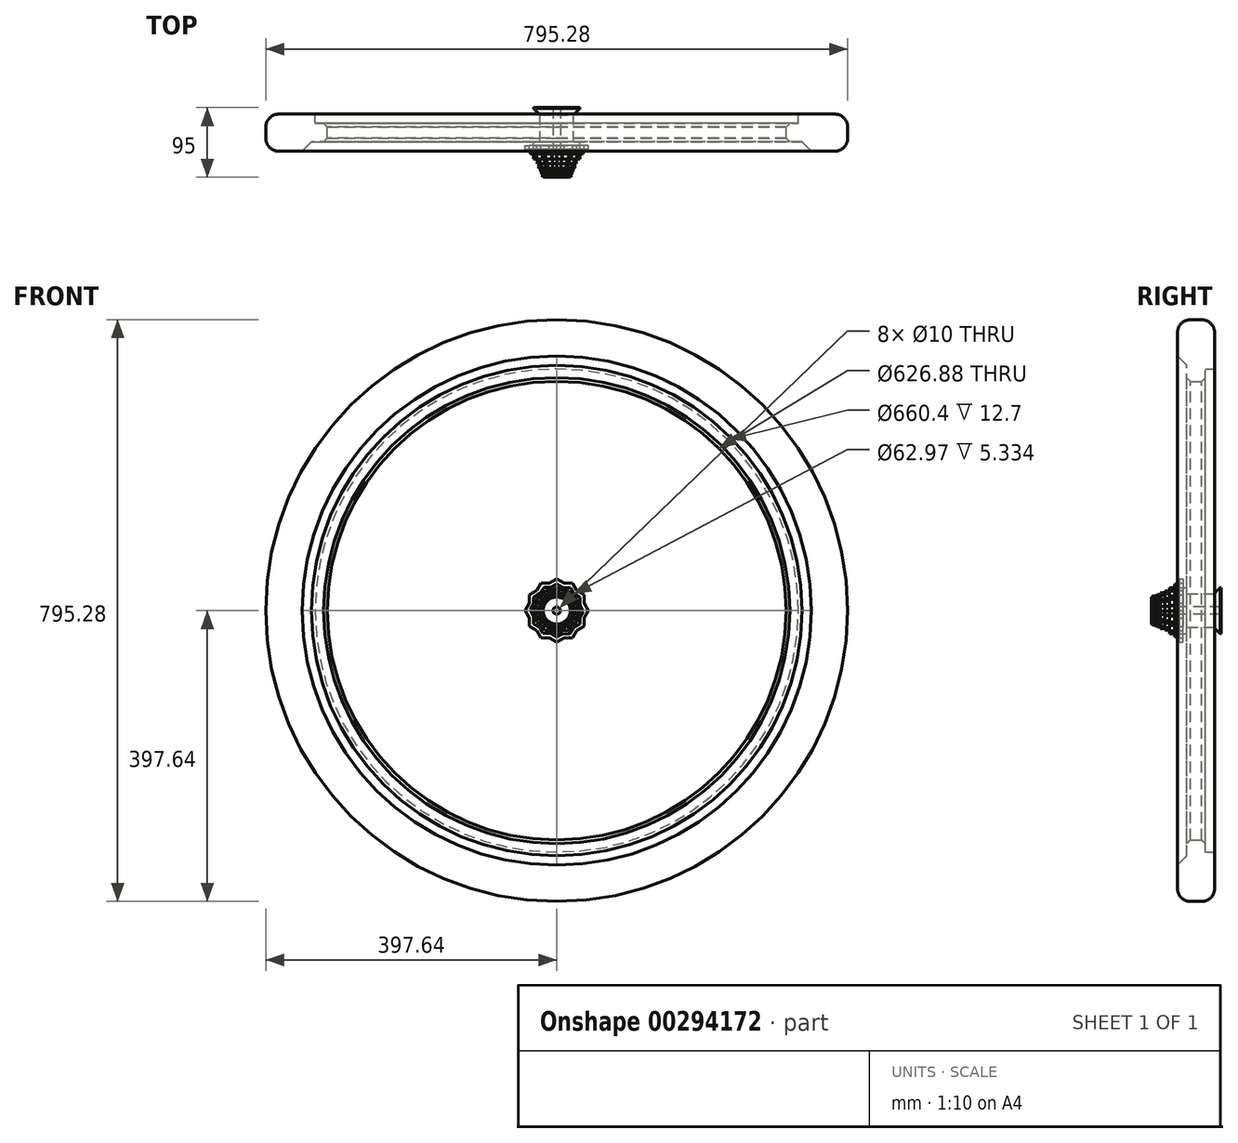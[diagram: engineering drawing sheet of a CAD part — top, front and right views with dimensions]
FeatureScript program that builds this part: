
annotation { "Feature Type Name" : "Feature", "Feature Type Description" : "" }
export const myFeature = defineFeature(function(context is Context, id is Id, definition is map)
    precondition{}
    {
        {
            var Q0;
            Q0=qCreatedBy(makeId("Front.planeOp"),FACE);
            var sketch = newSketch(context, id + "F0", { "sketchPlane" : qUnion([Q0])});
            skCircle(sketch, "E0", {"center": v(0, 0) * mm, "radius": 330.2 * mm});
            skCircle(sketch, "E1", {"center": v(0, 0) * mm, "radius": 313.44 * mm});
            skSolve(sketch);
        }
        {
            var Q0;
            Q0 = qSketchRegion(id + "F0", true);
            extrude(context, id + "F1", {"entities" : qUnion([Q0]), "endBound" : BoundingType.SYMMETRIC, "depth" : 25.4 * mm});
        }
        {
            var Q0;
            Q0=makeQuery(id+"F1.opExtrude","CAP_EDGE",EDGE,{"disambiguationData":[OSD([sQuery(id+"F0.wireOp",EDGE,"E1")])],"isStart":false});
            var Q1;
            Q1=makeQuery(id+"F1.opExtrude","CAP_EDGE",EDGE,{"disambiguationData":[OSD([sQuery(id+"F0.wireOp",EDGE,"E1")])],"isStart":true});
            chamfer(context, id + "F2", {"entities" : qUnion([Q0, Q1]), "width" : 5.08 * mm, "tangentPropagation" : true});
        }
        {
            var Q0;
            Q0=qCreatedBy(makeId("Front.planeOp"),FACE);
            var sketch = newSketch(context, id + "F3", { "sketchPlane" : qUnion([Q0])});
            skCircle(sketch, "E2", {"center": v(0, 0) * mm, "radius": 23.03 * mm});
            skSolve(sketch);
        }
        {
            var Q0;
            Q0 = qSketchRegion(id + "F3", true);
            extrude(context, id + "F4", {"entities" : qUnion([Q0]), "endBound" : BoundingType.SYMMETRIC, "depth" : 25.4 * mm});
        }
        {
            var Q0;
            Q0=makeQuery(id+"F4.opExtrude","CAP_FACE",FACE,{"disambiguationData":[OSD([sQuery(id+"F3.wireOp",EDGE,"E2")])],"isStart":true});
            var sketch = newSketch(context, id + "F5", { "sketchPlane" : qUnion([Q0])});
            skCircle(sketch, "E3", {"center": v(0, 0) * mm, "radius": 31.49 * mm});
            skSolve(sketch);
        }
        {
            var Q0;
            Q0 = qSketchRegion(id + "F5", true);
            extrude(context, id + "F6", {"entities" : qUnion([Q0]), "operationType" : NewBodyOperationType.ADD, "depth" : 21.59 * mm});
        }
        {
            var Q0;
            Q0=makeQuery(id+"F4.opExtrude","CAP_FACE",FACE,{"disambiguationData":[OSD([sQuery(id+"F3.wireOp",EDGE,"E2")])],"isStart":false});
            var sketch = newSketch(context, id + "F7", { "sketchPlane" : qUnion([Q0])});
            skCircle(sketch, "E4", {"center": v(0, 0) * mm, "radius": 31.48 * mm});
            skSolve(sketch);
        }
        {
            var Q0;
            Q0 = qSketchRegion(id + "F7", true);
            extrude(context, id + "F8", {"entities" : qUnion([Q0]), "operationType" : NewBodyOperationType.ADD, "depth" : 4.83 * mm});
        }
        {
            var Q0;
            Q0=makeQuery(id+"F6.opExtrude","CAP_EDGE",EDGE,{"disambiguationData":[OSD([sQuery(id+"F5.wireOp",EDGE,"E3")])],"isStart":true});
            chamfer(context, id + "F9", {"entities" : qUnion([Q0]), "width" : 20.32 * mm, "tangentPropagation" : true});
        }
        {
            var Q0;
            Q0=makeQuery(id+"F8.opExtrude","CAP_FACE",FACE,{"disambiguationData":[OSD([sQuery(id+"F7.wireOp",EDGE,"E4")])],"isStart":false});
            var sketch = newSketch(context, id + "F10", { "sketchPlane" : qUnion([Q0])});
            skCircle(sketch, "E5", {"center": v(0, 0) * mm, "radius": 18.57 * mm});
            skSolve(sketch);
        }
        {
            var Q0;
            Q0 = qSketchRegion(id + "F10", true);
            extrude(context, id + "F11", {"entities" : qUnion([Q0]), "operationType" : NewBodyOperationType.ADD, "depth" : 43.18 * mm});
        }
        {
            var Q0;
            Q0=makeQuery(id+"F8.opExtrude","CAP_FACE",FACE,{"disambiguationData":[OSD([sQuery(id+"F7.wireOp",EDGE,"E4")])],"isStart":false});
            var sketch = newSketch(context, id + "F12", { "sketchPlane" : qUnion([Q0])});
            skCircle(sketch, "E6.cCircle", {"center": v(0, 0) * mm, "radius": 37.52 * mm, "construction": true});
            skLineSegment(sketch, "E6.0", {"start": v(37.52, 21.66) * mm, "end": v(37.52, -21.66) * mm});
            skLineSegment(sketch, "E6.1", {"start": v(37.52, -21.66) * mm, "end": v(0, -43.33) * mm});
            skLineSegment(sketch, "E6.2", {"start": v(0, -43.33) * mm, "end": v(-37.52, -21.66) * mm});
            skLineSegment(sketch, "E6.3", {"start": v(-37.52, -21.66) * mm, "end": v(-37.52, 21.66) * mm});
            skLineSegment(sketch, "E6.4", {"start": v(-37.52, 21.66) * mm, "end": v(0, 43.33) * mm});
            skLineSegment(sketch, "E6.5", {"start": v(0, 43.33) * mm, "end": v(37.52, 21.66) * mm});
            skPoint(sketch, "E6.0.midPoint", {"position": v(37.52, 0) * mm});
            skLineSegment(sketch, "E7.0", {"start": v(21.66, 37.52) * mm, "end": v(43.33, 0) * mm});
            skLineSegment(sketch, "E7.1", {"start": v(43.33, 0) * mm, "end": v(21.66, -37.52) * mm});
            skLineSegment(sketch, "E7.2", {"start": v(21.66, -37.52) * mm, "end": v(-21.66, -37.52) * mm});
            skLineSegment(sketch, "E7.3", {"start": v(-21.66, -37.52) * mm, "end": v(-43.33, 0) * mm});
            skLineSegment(sketch, "E7.4", {"start": v(-43.33, 0) * mm, "end": v(-21.66, 37.52) * mm});
            skLineSegment(sketch, "E7.5", {"start": v(-21.66, 37.52) * mm, "end": v(21.66, 37.52) * mm});
            skPoint(sketch, "E7.0.midPoint", {"position": v(32.5, 18.76) * mm});
            skSolve(sketch);
        }
        {
            var Q0;
            Q0=makeQuery(id+"F12.imprint","IMPRINT",FACE,{"disambiguationData":[TD([[makeQuery(id+"F12.imprint","IMPRINT",EDGE,{"derivedFrom":makeQuery(id+"F8.opExtrude","CAP_EDGE",EDGE,{"disambiguationData":[OSD([sQuery(id+"F7.wireOp",EDGE,"E4")])],"isStart":false})}),-1.0]])]});
            var Q1;
            {var subQ0=sQuery(id+"F12.wireOp",EDGE,"E7.5");var subQ1=sQuery(id+"F12.wireOp",EDGE,"E6.5");var subQ2=makeQuery(id+"F12.imprint","INTERSECT",VERTEX,{"derivedFrom":[subQ1,subQ0]});Q1=makeQuery(id+"F12.imprint","IMPRINT",FACE,{"disambiguationData":[TD([[makeQuery(id+"F12.imprint","IMPRINT",EDGE,{"disambiguationData":[TD([[subQ2,-1.0]])],"derivedFrom":subQ1}),1.0]])]});}
            var Q2;
            {var subQ0=sQuery(id+"F12.wireOp",EDGE,"E7.4");var subQ1=sQuery(id+"F12.wireOp",EDGE,"E6.4");var subQ2=makeQuery(id+"F12.imprint","INTERSECT",VERTEX,{"derivedFrom":[subQ1,subQ0]});Q2=makeQuery(id+"F12.imprint","IMPRINT",FACE,{"disambiguationData":[TD([[makeQuery(id+"F12.imprint","IMPRINT",EDGE,{"disambiguationData":[TD([[subQ2,-1.0]])],"derivedFrom":subQ1}),1.0]])]});}
            var Q3;
            {var subQ0=sQuery(id+"F12.wireOp",EDGE,"E6.5");var subQ1=sQuery(id+"F12.wireOp",EDGE,"E6.4");var subQ2=makeQuery(id+"F12.imprint","INTERSECT",VERTEX,{"derivedFrom":[subQ1,subQ0]});Q3=makeQuery(id+"F12.imprint","IMPRINT",FACE,{"disambiguationData":[TD([[makeQuery(id+"F12.imprint","IMPRINT",EDGE,{"disambiguationData":[TD([[subQ2,1.0]])],"derivedFrom":subQ1}),-1.0]])]});}
            var Q4;
            {var subQ0=sQuery(id+"F12.wireOp",EDGE,"E6.4");var subQ1=sQuery(id+"F12.wireOp",EDGE,"E6.3");var subQ2=makeQuery(id+"F12.imprint","INTERSECT",VERTEX,{"derivedFrom":[subQ1,subQ0]});Q4=makeQuery(id+"F12.imprint","IMPRINT",FACE,{"disambiguationData":[TD([[makeQuery(id+"F12.imprint","IMPRINT",EDGE,{"disambiguationData":[TD([[subQ2,1.0]])],"derivedFrom":subQ1}),-1.0]])]});}
            var Q5;
            {var subQ0=sQuery(id+"F12.wireOp",EDGE,"E7.3");var subQ1=sQuery(id+"F12.wireOp",EDGE,"E6.3");var subQ2=makeQuery(id+"F12.imprint","INTERSECT",VERTEX,{"derivedFrom":[subQ1,subQ0]});Q5=makeQuery(id+"F12.imprint","IMPRINT",FACE,{"disambiguationData":[TD([[makeQuery(id+"F12.imprint","IMPRINT",EDGE,{"disambiguationData":[TD([[subQ2,-1.0]])],"derivedFrom":subQ1}),1.0]])]});}
            var Q6;
            {var subQ0=sQuery(id+"F12.wireOp",EDGE,"E6.3");var subQ1=sQuery(id+"F12.wireOp",EDGE,"E6.2");var subQ2=makeQuery(id+"F12.imprint","INTERSECT",VERTEX,{"derivedFrom":[subQ1,subQ0]});Q6=makeQuery(id+"F12.imprint","IMPRINT",FACE,{"disambiguationData":[TD([[makeQuery(id+"F12.imprint","IMPRINT",EDGE,{"disambiguationData":[TD([[subQ2,1.0]])],"derivedFrom":subQ1}),-1.0]])]});}
            var Q7;
            {var subQ0=sQuery(id+"F12.wireOp",EDGE,"E7.2");var subQ1=sQuery(id+"F12.wireOp",EDGE,"E6.2");var subQ2=makeQuery(id+"F12.imprint","INTERSECT",VERTEX,{"derivedFrom":[subQ1,subQ0]});Q7=makeQuery(id+"F12.imprint","IMPRINT",FACE,{"disambiguationData":[TD([[makeQuery(id+"F12.imprint","IMPRINT",EDGE,{"disambiguationData":[TD([[subQ2,-1.0]])],"derivedFrom":subQ1}),1.0]])]});}
            var Q8;
            {var subQ0=sQuery(id+"F12.wireOp",EDGE,"E6.2");var subQ1=sQuery(id+"F12.wireOp",EDGE,"E6.1");var subQ2=makeQuery(id+"F12.imprint","INTERSECT",VERTEX,{"derivedFrom":[subQ1,subQ0]});Q8=makeQuery(id+"F12.imprint","IMPRINT",FACE,{"disambiguationData":[TD([[makeQuery(id+"F12.imprint","IMPRINT",EDGE,{"disambiguationData":[TD([[subQ2,1.0]])],"derivedFrom":subQ1}),-1.0]])]});}
            var Q9;
            {var subQ0=sQuery(id+"F12.wireOp",EDGE,"E7.1");var subQ1=sQuery(id+"F12.wireOp",EDGE,"E6.1");var subQ2=makeQuery(id+"F12.imprint","INTERSECT",VERTEX,{"derivedFrom":[subQ1,subQ0]});Q9=makeQuery(id+"F12.imprint","IMPRINT",FACE,{"disambiguationData":[TD([[makeQuery(id+"F12.imprint","IMPRINT",EDGE,{"disambiguationData":[TD([[subQ2,-1.0]])],"derivedFrom":subQ1}),1.0]])]});}
            var Q10;
            {var subQ0=sQuery(id+"F12.wireOp",EDGE,"E6.1");var subQ1=sQuery(id+"F12.wireOp",EDGE,"E6.0");var subQ2=makeQuery(id+"F12.imprint","INTERSECT",VERTEX,{"derivedFrom":[subQ1,subQ0]});Q10=makeQuery(id+"F12.imprint","IMPRINT",FACE,{"disambiguationData":[TD([[makeQuery(id+"F12.imprint","IMPRINT",EDGE,{"disambiguationData":[TD([[subQ2,1.0]])],"derivedFrom":subQ1}),-1.0]])]});}
            var Q11;
            {var subQ0=sQuery(id+"F12.wireOp",EDGE,"E7.0");var subQ1=sQuery(id+"F12.wireOp",EDGE,"E6.0");var subQ2=makeQuery(id+"F12.imprint","INTERSECT",VERTEX,{"derivedFrom":[subQ1,subQ0]});Q11=makeQuery(id+"F12.imprint","IMPRINT",FACE,{"disambiguationData":[TD([[makeQuery(id+"F12.imprint","IMPRINT",EDGE,{"disambiguationData":[TD([[subQ2,-1.0]])],"derivedFrom":subQ1}),1.0]])]});}
            var Q12;
            {var subQ0=sQuery(id+"F12.wireOp",EDGE,"E6.5");var subQ1=sQuery(id+"F12.wireOp",EDGE,"E6.0");var subQ2=makeQuery(id+"F12.imprint","INTERSECT",VERTEX,{"derivedFrom":[subQ1,subQ0]});Q12=makeQuery(id+"F12.imprint","IMPRINT",FACE,{"disambiguationData":[TD([[makeQuery(id+"F12.imprint","IMPRINT",EDGE,{"disambiguationData":[TD([[subQ2,-1.0]])],"derivedFrom":subQ1}),-1.0]])]});}
            extrude(context, id + "F13", {"entities" : qUnion([Q0, Q1, Q2, Q3, Q4, Q5, Q6, Q7, Q8, Q9, Q10, Q11, Q12]), "depth" : 5.33 * mm});
        }
        {
            var Q0;
            Q0=makeQuery(id+"F13.opExtrude","CAP_FACE",FACE,{"disambiguationData":[OSD([sQuery(id+"F7.wireOp",EDGE,"E4"),sQuery(id+"F12.wireOp",EDGE,"E6.0"),sQuery(id+"F12.wireOp",EDGE,"E6.1"),sQuery(id+"F12.wireOp",EDGE,"E6.2"),sQuery(id+"F12.wireOp",EDGE,"E6.3"),sQuery(id+"F12.wireOp",EDGE,"E6.4"),sQuery(id+"F12.wireOp",EDGE,"E6.5"),sQuery(id+"F12.wireOp",EDGE,"E7.0"),sQuery(id+"F12.wireOp",EDGE,"E7.1"),sQuery(id+"F12.wireOp",EDGE,"E7.2"),sQuery(id+"F12.wireOp",EDGE,"E7.3"),sQuery(id+"F12.wireOp",EDGE,"E7.4"),sQuery(id+"F12.wireOp",EDGE,"E7.5")])],"isStart":false});
            var sketch = newSketch(context, id + "F14", { "sketchPlane" : qUnion([Q0])});
            skCircle(sketch, "E8.cCircle", {"center": v(0, 0) * mm, "radius": 31.48 * mm, "construction": true});
            skLineSegment(sketch, "E8.0", {"start": v(31.48, 18.18) * mm, "end": v(31.48, -18.18) * mm});
            skLineSegment(sketch, "E8.1", {"start": v(31.48, -18.18) * mm, "end": v(0, -36.36) * mm});
            skLineSegment(sketch, "E8.2", {"start": v(0, -36.36) * mm, "end": v(-31.48, -18.18) * mm});
            skLineSegment(sketch, "E8.3", {"start": v(-31.48, -18.18) * mm, "end": v(-31.48, 18.18) * mm});
            skLineSegment(sketch, "E8.4", {"start": v(-31.48, 18.18) * mm, "end": v(0, 36.36) * mm});
            skLineSegment(sketch, "E8.5", {"start": v(0, 36.36) * mm, "end": v(31.48, 18.18) * mm});
            skPoint(sketch, "E8.0.midPoint", {"position": v(31.48, 0) * mm});
            skLineSegment(sketch, "E9.0", {"start": v(19.11, 30.93) * mm, "end": v(36.34, -1.09) * mm});
            skLineSegment(sketch, "E9.1", {"start": v(36.34, -1.09) * mm, "end": v(17.23, -32.01) * mm});
            skLineSegment(sketch, "E9.2", {"start": v(17.23, -32.01) * mm, "end": v(-19.11, -30.93) * mm});
            skLineSegment(sketch, "E9.3", {"start": v(-19.11, -30.93) * mm, "end": v(-36.34, 1.09) * mm});
            skLineSegment(sketch, "E9.4", {"start": v(-36.34, 1.09) * mm, "end": v(-17.23, 32.01) * mm});
            skLineSegment(sketch, "E9.5", {"start": v(-17.23, 32.01) * mm, "end": v(19.11, 30.93) * mm});
            skPoint(sketch, "E9.0.midPoint", {"position": v(27.73, 14.92) * mm});
            skSolve(sketch);
        }
        {
            var Q0;
            Q0 = qSketchRegion(id + "F14", true);
            extrude(context, id + "F15", {"entities" : qUnion([Q0]), "depth" : 6.35 * mm});
        }
        {
            var Q0;
            Q0=makeQuery(id+"F15.opExtrude","CAP_FACE",FACE,{"disambiguationData":[OSD([sQuery(id+"F14.wireOp",EDGE,"E8.0"),sQuery(id+"F14.wireOp",EDGE,"E8.1"),sQuery(id+"F14.wireOp",EDGE,"E8.2"),sQuery(id+"F14.wireOp",EDGE,"E8.3"),sQuery(id+"F14.wireOp",EDGE,"E8.4"),sQuery(id+"F14.wireOp",EDGE,"E8.5"),sQuery(id+"F14.wireOp",EDGE,"E9.0"),sQuery(id+"F14.wireOp",EDGE,"E9.1"),sQuery(id+"F14.wireOp",EDGE,"E9.2"),sQuery(id+"F14.wireOp",EDGE,"E9.3"),sQuery(id+"F14.wireOp",EDGE,"E9.4"),sQuery(id+"F14.wireOp",EDGE,"E9.5")])],"isStart":false});
            var sketch = newSketch(context, id + "F16", { "sketchPlane" : qUnion([Q0])});
            skCircle(sketch, "E10.cCircle", {"center": v(0, 0) * mm, "radius": 27.32 * mm, "construction": true});
            skLineSegment(sketch, "E10.0", {"start": v(0.15, 31.54) * mm, "end": v(27.4, 15.64) * mm});
            skLineSegment(sketch, "E10.1", {"start": v(27.4, 15.64) * mm, "end": v(27.24, -15.9) * mm});
            skLineSegment(sketch, "E10.2", {"start": v(27.24, -15.9) * mm, "end": v(-0.15, -31.54) * mm});
            skLineSegment(sketch, "E10.3", {"start": v(-0.15, -31.54) * mm, "end": v(-27.4, -15.64) * mm});
            skLineSegment(sketch, "E10.4", {"start": v(-27.4, -15.64) * mm, "end": v(-27.24, 15.9) * mm});
            skLineSegment(sketch, "E10.5", {"start": v(-27.24, 15.9) * mm, "end": v(0.15, 31.54) * mm});
            skPoint(sketch, "E10.0.midPoint", {"position": v(13.77, 23.6) * mm});
            skLineSegment(sketch, "E11.0", {"start": v(16.27, 27.02) * mm, "end": v(31.54, -0.58) * mm});
            skLineSegment(sketch, "E11.1", {"start": v(31.54, -0.58) * mm, "end": v(15.27, -27.6) * mm});
            skLineSegment(sketch, "E11.2", {"start": v(15.27, -27.6) * mm, "end": v(-16.27, -27.02) * mm});
            skLineSegment(sketch, "E11.3", {"start": v(-16.27, -27.02) * mm, "end": v(-31.54, 0.58) * mm});
            skLineSegment(sketch, "E11.4", {"start": v(-31.54, 0.58) * mm, "end": v(-15.27, 27.6) * mm});
            skLineSegment(sketch, "E11.5", {"start": v(-15.27, 27.6) * mm, "end": v(16.27, 27.02) * mm});
            skPoint(sketch, "E11.0.midPoint", {"position": v(23.9, 13.22) * mm});
            skSolve(sketch);
        }
        {
            var Q0;
            Q0 = qSketchRegion(id + "F16", true);
            extrude(context, id + "F17", {"entities" : qUnion([Q0]), "depth" : 6.86 * mm});
        }
        {
            var Q0;
            Q0=makeQuery(id+"F17.opExtrude","CAP_FACE",FACE,{"disambiguationData":[OSD([sQuery(id+"F16.wireOp",EDGE,"E10.0"),sQuery(id+"F16.wireOp",EDGE,"E10.1"),sQuery(id+"F16.wireOp",EDGE,"E10.2"),sQuery(id+"F16.wireOp",EDGE,"E10.3"),sQuery(id+"F16.wireOp",EDGE,"E10.4"),sQuery(id+"F16.wireOp",EDGE,"E10.5"),sQuery(id+"F16.wireOp",EDGE,"E11.0"),sQuery(id+"F16.wireOp",EDGE,"E11.1"),sQuery(id+"F16.wireOp",EDGE,"E11.2"),sQuery(id+"F16.wireOp",EDGE,"E11.3"),sQuery(id+"F16.wireOp",EDGE,"E11.4"),sQuery(id+"F16.wireOp",EDGE,"E11.5")])],"isStart":false});
            var sketch = newSketch(context, id + "F18", { "sketchPlane" : qUnion([Q0])});
            skCircle(sketch, "E12.cCircle", {"center": v(0, 0) * mm, "radius": 23.24 * mm, "construction": true});
            skLineSegment(sketch, "E12.0", {"start": v(0.45, 26.83) * mm, "end": v(23.46, 13.03) * mm});
            skLineSegment(sketch, "E12.1", {"start": v(23.46, 13.03) * mm, "end": v(23.01, -13.8) * mm});
            skLineSegment(sketch, "E12.2", {"start": v(23.01, -13.8) * mm, "end": v(-0.45, -26.83) * mm});
            skLineSegment(sketch, "E12.3", {"start": v(-0.45, -26.83) * mm, "end": v(-23.46, -13.03) * mm});
            skLineSegment(sketch, "E12.4", {"start": v(-23.46, -13.03) * mm, "end": v(-23.01, 13.8) * mm});
            skLineSegment(sketch, "E12.5", {"start": v(-23.01, 13.8) * mm, "end": v(0.45, 26.83) * mm});
            skPoint(sketch, "E12.0.midPoint", {"position": v(11.96, 19.93) * mm});
            skLineSegment(sketch, "E13.0", {"start": v(13.8, 23.01) * mm, "end": v(26.83, -0.45) * mm});
            skLineSegment(sketch, "E13.1", {"start": v(26.83, -0.45) * mm, "end": v(13.03, -23.46) * mm});
            skLineSegment(sketch, "E13.2", {"start": v(13.03, -23.46) * mm, "end": v(-13.8, -23.01) * mm});
            skLineSegment(sketch, "E13.3", {"start": v(-13.8, -23.01) * mm, "end": v(-26.83, 0.45) * mm});
            skLineSegment(sketch, "E13.4", {"start": v(-26.83, 0.45) * mm, "end": v(-13.03, 23.46) * mm});
            skLineSegment(sketch, "E13.5", {"start": v(-13.03, 23.46) * mm, "end": v(13.8, 23.01) * mm});
            skPoint(sketch, "E13.0.midPoint", {"position": v(20.32, 11.28) * mm});
            skSolve(sketch);
        }
        {
            var Q0;
            Q0 = qSketchRegion(id + "F18", true);
            extrude(context, id + "F19", {"entities" : qUnion([Q0]), "depth" : 6.35 * mm});
        }
        {
            var Q0;
            Q0=makeQuery(id+"F19.opExtrude","CAP_FACE",FACE,{"disambiguationData":[OSD([sQuery(id+"F18.wireOp",EDGE,"E12.0"),sQuery(id+"F18.wireOp",EDGE,"E12.1"),sQuery(id+"F18.wireOp",EDGE,"E12.2"),sQuery(id+"F18.wireOp",EDGE,"E12.3"),sQuery(id+"F18.wireOp",EDGE,"E12.4"),sQuery(id+"F18.wireOp",EDGE,"E12.5"),sQuery(id+"F18.wireOp",EDGE,"E13.0"),sQuery(id+"F18.wireOp",EDGE,"E13.1"),sQuery(id+"F18.wireOp",EDGE,"E13.2"),sQuery(id+"F18.wireOp",EDGE,"E13.3"),sQuery(id+"F18.wireOp",EDGE,"E13.4"),sQuery(id+"F18.wireOp",EDGE,"E13.5")])],"isStart":false});
            var sketch = newSketch(context, id + "F20", { "sketchPlane" : qUnion([Q0])});
            skCircle(sketch, "E14.cCircle", {"center": v(0, 0) * mm, "radius": 21.2 * mm, "construction": true});
            skLineSegment(sketch, "E14.0", {"start": v(12.5, 21.04) * mm, "end": v(24.47, -0.3) * mm});
            skLineSegment(sketch, "E14.1", {"start": v(24.47, -0.3) * mm, "end": v(11.97, -21.34) * mm});
            skLineSegment(sketch, "E14.2", {"start": v(11.97, -21.34) * mm, "end": v(-12.5, -21.04) * mm});
            skLineSegment(sketch, "E14.3", {"start": v(-12.5, -21.04) * mm, "end": v(-24.47, 0.3) * mm});
            skLineSegment(sketch, "E14.4", {"start": v(-24.47, 0.3) * mm, "end": v(-11.97, 21.34) * mm});
            skLineSegment(sketch, "E14.5", {"start": v(-11.97, 21.34) * mm, "end": v(12.5, 21.04) * mm});
            skPoint(sketch, "E14.0.midPoint", {"position": v(18.48, 10.37) * mm});
            skLineSegment(sketch, "E15.0", {"start": v(-0.01, 24.47) * mm, "end": v(21.19, 12.24) * mm});
            skLineSegment(sketch, "E15.1", {"start": v(21.19, 12.24) * mm, "end": v(21.2, -12.23) * mm});
            skLineSegment(sketch, "E15.2", {"start": v(21.2, -12.23) * mm, "end": v(0.01, -24.47) * mm});
            skLineSegment(sketch, "E15.3", {"start": v(0.01, -24.47) * mm, "end": v(-21.19, -12.24) * mm});
            skLineSegment(sketch, "E15.4", {"start": v(-21.19, -12.24) * mm, "end": v(-21.2, 12.23) * mm});
            skLineSegment(sketch, "E15.5", {"start": v(-21.2, 12.23) * mm, "end": v(-0.01, 24.47) * mm});
            skPoint(sketch, "E15.0.midPoint", {"position": v(10.59, 18.36) * mm});
            skSolve(sketch);
        }
        {
            var Q0;
            Q0 = qSketchRegion(id + "F20", true);
            extrude(context, id + "F21", {"entities" : qUnion([Q0]), "depth" : 6.35 * mm});
        }
        {
            var Q0;
            Q0=makeQuery(id+"F21.opExtrude","CAP_FACE",FACE,{"disambiguationData":[OSD([sQuery(id+"F20.wireOp",EDGE,"E14.0"),sQuery(id+"F20.wireOp",EDGE,"E14.1"),sQuery(id+"F20.wireOp",EDGE,"E14.2"),sQuery(id+"F20.wireOp",EDGE,"E14.3"),sQuery(id+"F20.wireOp",EDGE,"E14.4"),sQuery(id+"F20.wireOp",EDGE,"E14.5"),sQuery(id+"F20.wireOp",EDGE,"E15.0"),sQuery(id+"F20.wireOp",EDGE,"E15.1"),sQuery(id+"F20.wireOp",EDGE,"E15.2"),sQuery(id+"F20.wireOp",EDGE,"E15.3"),sQuery(id+"F20.wireOp",EDGE,"E15.4"),sQuery(id+"F20.wireOp",EDGE,"E15.5")])],"isStart":false});
            var sketch = newSketch(context, id + "F22", { "sketchPlane" : qUnion([Q0])});
            skCircle(sketch, "E16.cCircle", {"center": v(0, 0) * mm, "radius": 19.03 * mm, "construction": true});
            skLineSegment(sketch, "E16.0", {"start": v(11.41, 18.77) * mm, "end": v(21.96, -0.5) * mm});
            skLineSegment(sketch, "E16.1", {"start": v(21.96, -0.5) * mm, "end": v(10.55, -19.27) * mm});
            skLineSegment(sketch, "E16.2", {"start": v(10.55, -19.27) * mm, "end": v(-11.41, -18.77) * mm});
            skLineSegment(sketch, "E16.3", {"start": v(-11.41, -18.77) * mm, "end": v(-21.96, 0.5) * mm});
            skLineSegment(sketch, "E16.4", {"start": v(-21.96, 0.5) * mm, "end": v(-10.55, 19.27) * mm});
            skLineSegment(sketch, "E16.5", {"start": v(-10.55, 19.27) * mm, "end": v(11.41, 18.77) * mm});
            skPoint(sketch, "E16.0.midPoint", {"position": v(16.69, 9.14) * mm});
            skLineSegment(sketch, "E17.0", {"start": v(-0.03, 21.97) * mm, "end": v(19, 11.01) * mm});
            skLineSegment(sketch, "E17.1", {"start": v(19, 11.01) * mm, "end": v(19.04, -10.95) * mm});
            skLineSegment(sketch, "E17.2", {"start": v(19.04, -10.95) * mm, "end": v(0.03, -21.97) * mm});
            skLineSegment(sketch, "E17.3", {"start": v(0.03, -21.97) * mm, "end": v(-19, -11.01) * mm});
            skLineSegment(sketch, "E17.4", {"start": v(-19, -11.01) * mm, "end": v(-19.04, 10.95) * mm});
            skLineSegment(sketch, "E17.5", {"start": v(-19.04, 10.95) * mm, "end": v(-0.03, 21.97) * mm});
            skPoint(sketch, "E17.0.midPoint", {"position": v(9.49, 16.5) * mm});
            skSolve(sketch);
        }
        {
            var Q0;
            Q0 = qSketchRegion(id + "F22", true);
            extrude(context, id + "F23", {"entities" : qUnion([Q0]), "depth" : 4.57 * mm});
        }
        {
            var Q0;
            Q0=makeQuery(id+"F23.opExtrude","CAP_FACE",FACE,{"disambiguationData":[OSD([sQuery(id+"F22.wireOp",EDGE,"E16.0"),sQuery(id+"F22.wireOp",EDGE,"E16.1"),sQuery(id+"F22.wireOp",EDGE,"E16.2"),sQuery(id+"F22.wireOp",EDGE,"E16.3"),sQuery(id+"F22.wireOp",EDGE,"E16.4"),sQuery(id+"F22.wireOp",EDGE,"E16.5"),sQuery(id+"F22.wireOp",EDGE,"E17.0"),sQuery(id+"F22.wireOp",EDGE,"E17.1"),sQuery(id+"F22.wireOp",EDGE,"E17.2"),sQuery(id+"F22.wireOp",EDGE,"E17.3"),sQuery(id+"F22.wireOp",EDGE,"E17.4"),sQuery(id+"F22.wireOp",EDGE,"E17.5")])],"isStart":false});
            var sketch = newSketch(context, id + "F24", { "sketchPlane" : qUnion([Q0])});
            skCircle(sketch, "E18.cCircle", {"center": v(0, 0) * mm, "radius": 17.95 * mm, "construction": true});
            skLineSegment(sketch, "E18.0", {"start": v(0, 20.72) * mm, "end": v(17.94, 10.37) * mm});
            skLineSegment(sketch, "E18.1", {"start": v(17.94, 10.37) * mm, "end": v(17.95, -10.35) * mm});
            skLineSegment(sketch, "E18.2", {"start": v(17.95, -10.35) * mm, "end": v(0, -20.72) * mm});
            skLineSegment(sketch, "E18.3", {"start": v(0, -20.72) * mm, "end": v(-17.94, -10.37) * mm});
            skLineSegment(sketch, "E18.4", {"start": v(-17.94, -10.37) * mm, "end": v(-17.95, 10.35) * mm});
            skLineSegment(sketch, "E18.5", {"start": v(-17.95, 10.35) * mm, "end": v(0, 20.72) * mm});
            skPoint(sketch, "E18.0.midPoint", {"position": v(8.97, 15.55) * mm});
            skLineSegment(sketch, "E19.0", {"start": v(10.69, 17.76) * mm, "end": v(20.72, -0.38) * mm});
            skLineSegment(sketch, "E19.1", {"start": v(20.72, -0.38) * mm, "end": v(10.03, -18.13) * mm});
            skLineSegment(sketch, "E19.2", {"start": v(10.03, -18.13) * mm, "end": v(-10.69, -17.76) * mm});
            skLineSegment(sketch, "E19.3", {"start": v(-10.69, -17.76) * mm, "end": v(-20.72, 0.38) * mm});
            skLineSegment(sketch, "E19.4", {"start": v(-20.72, 0.38) * mm, "end": v(-10.03, 18.13) * mm});
            skLineSegment(sketch, "E19.5", {"start": v(-10.03, 18.13) * mm, "end": v(10.69, 17.76) * mm});
            skPoint(sketch, "E19.0.midPoint", {"position": v(15.7, 8.69) * mm});
            skSolve(sketch);
        }
        {
            var Q0;
            Q0 = qSketchRegion(id + "F24", true);
            extrude(context, id + "F25", {"entities" : qUnion([Q0]), "depth" : 3.3 * mm});
        }
        {
            var Q0;
            Q0=makeQuery(id+"F25.opExtrude","CAP_FACE",FACE,{"disambiguationData":[OSD([sQuery(id+"F24.wireOp",EDGE,"E18.0"),sQuery(id+"F24.wireOp",EDGE,"E18.1"),sQuery(id+"F24.wireOp",EDGE,"E18.2"),sQuery(id+"F24.wireOp",EDGE,"E18.3"),sQuery(id+"F24.wireOp",EDGE,"E18.4"),sQuery(id+"F24.wireOp",EDGE,"E18.5"),sQuery(id+"F24.wireOp",EDGE,"E19.0"),sQuery(id+"F24.wireOp",EDGE,"E19.1"),sQuery(id+"F24.wireOp",EDGE,"E19.2"),sQuery(id+"F24.wireOp",EDGE,"E19.3"),sQuery(id+"F24.wireOp",EDGE,"E19.4"),sQuery(id+"F24.wireOp",EDGE,"E19.5")])],"isStart":false});
            var sketch = newSketch(context, id + "F26", { "sketchPlane" : qUnion([Q0])});
            skCircle(sketch, "E20.cCircle", {"center": v(0, 0) * mm, "radius": 16.94 * mm, "construction": true});
            skLineSegment(sketch, "E20.0", {"start": v(0.05, 19.56) * mm, "end": v(16.97, 9.74) * mm});
            skLineSegment(sketch, "E20.1", {"start": v(16.97, 9.74) * mm, "end": v(16.92, -9.83) * mm});
            skLineSegment(sketch, "E20.2", {"start": v(16.92, -9.83) * mm, "end": v(-0.05, -19.56) * mm});
            skLineSegment(sketch, "E20.3", {"start": v(-0.05, -19.56) * mm, "end": v(-16.97, -9.74) * mm});
            skLineSegment(sketch, "E20.4", {"start": v(-16.97, -9.74) * mm, "end": v(-16.92, 9.83) * mm});
            skLineSegment(sketch, "E20.5", {"start": v(-16.92, 9.83) * mm, "end": v(0.05, 19.56) * mm});
            skPoint(sketch, "E20.0.midPoint", {"position": v(8.5, 14.65) * mm});
            skLineSegment(sketch, "E21.0", {"start": v(10.23, 16.67) * mm, "end": v(19.56, -0.52) * mm});
            skLineSegment(sketch, "E21.1", {"start": v(19.56, -0.52) * mm, "end": v(9.32, -17.2) * mm});
            skLineSegment(sketch, "E21.2", {"start": v(9.32, -17.2) * mm, "end": v(-10.23, -16.67) * mm});
            skLineSegment(sketch, "E21.3", {"start": v(-10.23, -16.67) * mm, "end": v(-19.56, 0.52) * mm});
            skLineSegment(sketch, "E21.4", {"start": v(-19.56, 0.52) * mm, "end": v(-9.32, 17.2) * mm});
            skLineSegment(sketch, "E21.5", {"start": v(-9.32, 17.2) * mm, "end": v(10.23, 16.67) * mm});
            skPoint(sketch, "E21.0.midPoint", {"position": v(14.9, 8.07) * mm});
            skSolve(sketch);
        }
        {
            var Q0;
            Q0 = qSketchRegion(id + "F26", true);
            extrude(context, id + "F27", {"entities" : qUnion([Q0]), "depth" : 3.9 * mm});
        }
        {
            var Q0;
            Q0=makeQuery(id+"F11.opExtrude","CAP_FACE",FACE,{"disambiguationData":[OSD([sQuery(id+"F10.wireOp",EDGE,"E5")])],"isStart":false});
            var sketch = newSketch(context, id + "F28", { "sketchPlane" : qUnion([Q0])});
            skCircle(sketch, "E22", {"center": v(0, 0) * mm, "radius": 5 * mm});
            skSolve(sketch);
        }
        {
            var Q0;
            Q0 = qSketchRegion(id + "F28", true);
            extrude(context, id + "F29", {"entities" : qUnion([Q0]), "operationType" : NewBodyOperationType.REMOVE, "oppositeDirection" : true, "depth" : 118.1 * mm});
        }
        {
            var Q0;
            Q0=qCreatedBy(makeId("Front.planeOp"),FACE);
            var sketch = newSketch(context, id + "F30", { "sketchPlane" : qUnion([Q0])});
            skCircle(sketch, "E23", {"center": v(0, 0) * mm, "radius": 330.2 * mm});
            skCircle(sketch, "E24", {"center": v(0, 0) * mm, "radius": 397.64 * mm});
            skSolve(sketch);
        }
        {
            var Q0;
            Q0 = qSketchRegion(id + "F30", true);
            extrude(context, id + "F31", {"entities" : qUnion([Q0]), "operationType" : NewBodyOperationType.ADD, "endBound" : BoundingType.SYMMETRIC, "depth" : 50.8 * mm});
        }
        {
            var Q0;
            Q0=makeQuery(id+"F31.opExtrude","CAP_EDGE",EDGE,{"disambiguationData":[OSD([sQuery(id+"F30.wireOp",EDGE,"E23")])],"isStart":false});
            chamfer(context, id + "F32", {"entities" : qUnion([Q0]), "width" : 17.78 * mm, "tangentPropagation" : true});
        }
        {
            var Q0;
            Q0=makeQuery(id+"F31.opExtrude","CAP_EDGE",EDGE,{"disambiguationData":[OSD([sQuery(id+"F30.wireOp",EDGE,"E24")])],"isStart":false});
            var Q1;
            Q1=makeQuery(id+"F31.opExtrude","CAP_EDGE",EDGE,{"disambiguationData":[OSD([sQuery(id+"F30.wireOp",EDGE,"E24")])],"isStart":true});
            fillet(context, id + "F33", {"entities" : qUnion([Q0, Q1]), "radius" : 17.78 * mm, "tangentPropagation" : true, "allowEdgeOverflow" : false});
        }
    });
